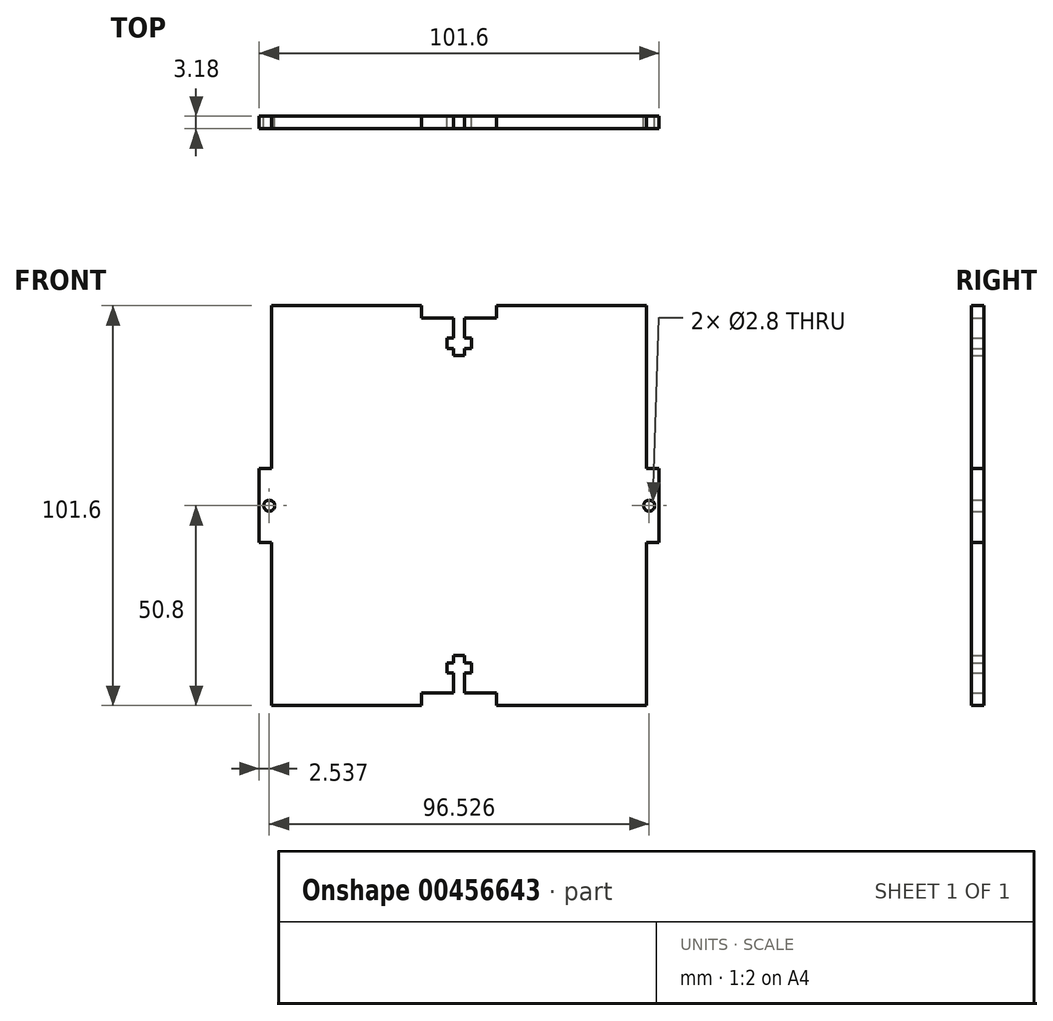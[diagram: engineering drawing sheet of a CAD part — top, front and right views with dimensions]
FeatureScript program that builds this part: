
annotation { "Feature Type Name" : "Feature", "Feature Type Description" : "" }
export const myFeature = defineFeature(function(context is Context, id is Id, definition is map)
    precondition{}
    {
        {
            var Q0;
            Q0=qCreatedBy(makeId("Front.planeOp"),FACE);
            var sketch = newSketch(context, id + "F0", { "sketchPlane" : qUnion([Q0])});
            skLineSegment(sketch, "E0.bottom", {"start": v(47.62, -50.8) * mm, "end": v(9.52, -50.8) * mm});
            skLineSegment(sketch, "E0.top", {"start": v(47.62, 50.8) * mm, "end": v(9.52, 50.8) * mm});
            skLineSegment(sketch, "E0.left", {"start": v(50.8, -9.4) * mm, "end": v(50.8, 9.4) * mm});
            skLineSegment(sketch, "E0.right", {"start": v(-50.8, -9.4) * mm, "end": v(-50.8, 9.4) * mm});
            skPoint(sketch, "E0.middle", {"position": v(0, 0) * mm});
            skLineSegment(sketch, "E1.top", {"start": v(-50.8, 9.4) * mm, "end": v(-47.62, 9.4) * mm});
            skLineSegment(sketch, "E1.right", {"start": v(-47.62, 50.8) * mm, "end": v(-47.62, 9.4) * mm});
            skLineSegment(sketch, "E2.top", {"start": v(-50.8, -9.4) * mm, "end": v(-47.62, -9.4) * mm});
            skLineSegment(sketch, "E2.right", {"start": v(-47.62, -50.8) * mm, "end": v(-47.62, -9.4) * mm});
            skLineSegment(sketch, "E3", {"start": v(-72, 0) * mm, "end": v(70.87, 0) * mm, "construction": true});
            skPoint(sketch, "E3.endSnap0", {"position": v(-50.8, 0) * mm});
            skPoint(sketch, "E4.orphan", {"position": v(-50.8, 50.8) * mm});
            skPoint(sketch, "E5.orphan", {"position": v(-50.8, -50.8) * mm});
            skLineSegment(sketch, "E6", {"start": v(0, 50.8) * mm, "end": v(0, -50.8) * mm, "construction": true});
            skLineSegment(sketch, "E7.MirrorCS", {"start": v(47.62, 50.8) * mm, "end": v(47.62, 9.4) * mm});
            skLineSegment(sketch, "E8.MirrorCS", {"start": v(50.8, 9.4) * mm, "end": v(47.63, 9.4) * mm});
            skLineSegment(sketch, "E9.MirrorCS", {"start": v(50.8, -9.4) * mm, "end": v(47.63, -9.4) * mm});
            skLineSegment(sketch, "E10.MirrorCS", {"start": v(47.62, -50.8) * mm, "end": v(47.62, -9.4) * mm});
            skPoint(sketch, "E11.orphan", {"position": v(50.8, 50.8) * mm});
            skPoint(sketch, "E12.orphan", {"position": v(50.8, -50.8) * mm});
            skLineSegment(sketch, "E13.top", {"start": v(-9.52, 47.62) * mm, "end": v(-1.4, 47.62) * mm});
            skLineSegment(sketch, "E13.left", {"start": v(-9.53, 50.8) * mm, "end": v(-9.53, 47.62) * mm});
            skLineSegment(sketch, "E13.right", {"start": v(9.53, 50.8) * mm, "end": v(9.53, 47.62) * mm});
            skLineSegment(sketch, "E14.top", {"start": v(-1.4, 38.1) * mm, "end": v(1.4, 38.1) * mm});
            skLineSegment(sketch, "E14.left", {"start": v(-1.4, 47.62) * mm, "end": v(-1.4, 42.54) * mm});
            skLineSegment(sketch, "E14.right", {"start": v(1.4, 47.62) * mm, "end": v(1.4, 42.54) * mm});
            skLineSegment(sketch, "E15.bottom", {"start": v(-3.13, 42.54) * mm, "end": v(-1.4, 42.54) * mm});
            skLineSegment(sketch, "E15.top", {"start": v(-3.12, 39.94) * mm, "end": v(-1.4, 39.94) * mm});
            skLineSegment(sketch, "E15.left", {"start": v(-3.12, 42.54) * mm, "end": v(-3.12, 39.94) * mm});
            skLineSegment(sketch, "E15.right", {"start": v(3.13, 42.54) * mm, "end": v(3.13, 39.94) * mm});
            skLineSegment(sketch, "E16.trimOffspring", {"start": v(1.4, 42.54) * mm, "end": v(3.13, 42.54) * mm});
            skLineSegment(sketch, "E17.trimOffspring", {"start": v(-1.4, 39.94) * mm, "end": v(-1.4, 38.1) * mm});
            skLineSegment(sketch, "E18.trimOffspring", {"start": v(1.4, 39.94) * mm, "end": v(3.13, 39.94) * mm});
            skLineSegment(sketch, "E19.trimOffspring", {"start": v(1.4, 39.94) * mm, "end": v(1.4, 38.1) * mm});
            skLineSegment(sketch, "E20.trimOffspring", {"start": v(1.4, 47.62) * mm, "end": v(9.53, 47.62) * mm});
            skLineSegment(sketch, "E21.trimOffspring", {"start": v(-9.52, 50.8) * mm, "end": v(-47.63, 50.8) * mm});
            skLineSegment(sketch, "E22.MirrorCS", {"start": v(1.4, -42.55) * mm, "end": v(3.12, -42.55) * mm});
            skLineSegment(sketch, "E23.MirrorCS", {"start": v(1.4, -39.95) * mm, "end": v(3.12, -39.95) * mm});
            skLineSegment(sketch, "E24.MirrorCS", {"start": v(-3.13, -42.55) * mm, "end": v(-3.13, -39.95) * mm});
            skLineSegment(sketch, "E25.MirrorCS", {"start": v(-3.13, -39.95) * mm, "end": v(-1.4, -39.95) * mm});
            skLineSegment(sketch, "E26.MirrorCS", {"start": v(-3.13, -42.55) * mm, "end": v(-1.4, -42.55) * mm});
            skLineSegment(sketch, "E27.MirrorCS", {"start": v(3.12, -42.55) * mm, "end": v(3.12, -39.95) * mm});
            skLineSegment(sketch, "E28.MirrorCS", {"start": v(-1.4, -39.95) * mm, "end": v(-1.4, -38.1) * mm});
            skLineSegment(sketch, "E29.MirrorCS", {"start": v(1.4, -39.95) * mm, "end": v(1.4, -38.1) * mm});
            skLineSegment(sketch, "E30.MirrorCS", {"start": v(-1.4, -38.1) * mm, "end": v(1.4, -38.1) * mm});
            skLineSegment(sketch, "E31.MirrorCS", {"start": v(9.52, -50.8) * mm, "end": v(9.52, -47.63) * mm});
            skLineSegment(sketch, "E32.MirrorCS", {"start": v(-9.53, -50.8) * mm, "end": v(-9.53, -47.63) * mm});
            skLineSegment(sketch, "E33.MirrorCS", {"start": v(-9.53, -47.63) * mm, "end": v(-1.4, -47.63) * mm});
            skLineSegment(sketch, "E34.MirrorCS", {"start": v(1.4, -47.63) * mm, "end": v(1.4, -42.55) * mm});
            skLineSegment(sketch, "E35.MirrorCS", {"start": v(-1.4, -47.63) * mm, "end": v(-1.4, -42.55) * mm});
            skLineSegment(sketch, "E36.MirrorCS", {"start": v(1.4, -47.63) * mm, "end": v(9.52, -47.63) * mm});
            skLineSegment(sketch, "E37.trimOffspring", {"start": v(-9.53, -50.8) * mm, "end": v(-47.62, -50.8) * mm});
            skCircle(sketch, "E38", {"center": v(-48.26, 0) * mm, "radius": 1.4 * mm});
            skCircle(sketch, "E39.MirrorC", {"center": v(48.26, 0) * mm, "radius": 1.4 * mm});
            skSolve(sketch);
        }
        {
            var Q0;
            Q0 = qSketchRegion(id + "F0", true);
            extrude(context, id + "F1", {"entities" : qUnion([Q0]), "depth" : 3.17 * mm});
        }
    });
